# Revit family: Bernhardt_Design-Seating-Lounge-Belmont
name_source: partatom
category: Furniture
revit_build: Autodesk Revit 2016 (Build: 20150714_1515(x64)
units: mm (PartAtom-declared; Revit-internal decimal feet)

## family parameters
Always vertical = Yes
Cut with Voids When Loaded = No
OmniClass Number = 23.40.20.00
OmniClass Title = General Furniture and Specialties
Room Calculation Point = No
Shared = No
Work Plane-Based = No

## types (10) — shared parameters
Manufacturer = Bernhardt Design
Model = Belmont
URL = http://www.bernhardtdesign.com

## per-type parameters (varying)
| type | Catalog | Metal base | Metal base on | SKU | Wood base on |
| Belmont - 3401 Ash Base | 3401 | <By Category> | No | 3401 | Yes |
| Belmont - 3402 Polished Base | 3402 | Aluminum - Polished | Yes | 3402 | No |
| Belmont - 3402WH Satin White Base | 3402WH | Aluminum - Satin White Powdercoat | Yes | 3402WH | No |
| Belmont - 3402EC Ecru Base | 3402EC | Aluminum - Ecru Powdercoat | Yes | 3402EC | No |
| Belmont - 3402LA Latte Base | 3402LA | Aluminum - Latte Powdercoat | Yes | 3402LA | No |
| Belmont - 3402GR Graphite Base | 3402GR | Aluminum - Graphite Powdercoat | Yes | 3402GR | No |
| Belmont - 3402BZ Bronze Base | 3402BZ | Aluminum - Bronze Powdercoat | Yes | 3402BZ | No |
| Belmont - 3402IG Iron Grey Base | 3402IG | Aluminum - Iron Grey Powdercoat | Yes | 3402IG | No |
| Belmont - 3402RD Black Red Base | 3402RD | Aluminum - Black Red Powdercoat | Yes | 3402RD | No |
| Belmont - 3402BK Matte Black Base | 3402BK | Aluminum - Matte Black Powdercoat | Yes | 3402BK | No |

## geometry (parser evidence)
native form markers: Sweep x8
no freeform markers — native parametric forms only
